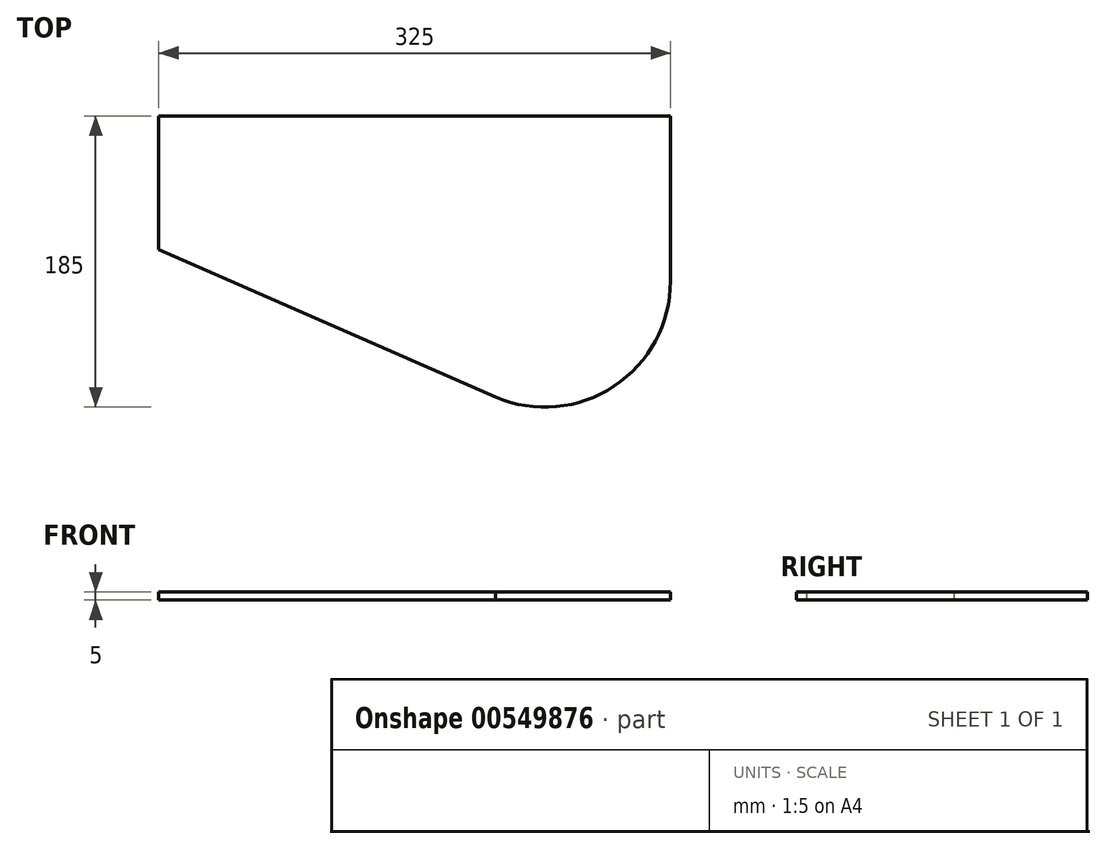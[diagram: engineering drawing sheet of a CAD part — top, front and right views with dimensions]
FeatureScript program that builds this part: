
annotation { "Feature Type Name" : "Feature", "Feature Type Description" : "" }
export const myFeature = defineFeature(function(context is Context, id is Id, definition is map)
    precondition{}
    {
        {
            var Q0;
            Q0=qCreatedBy(makeId("Top.planeOp"),FACE);
            var sketch = newSketch(context, id + "F0", { "sketchPlane" : qUnion([Q0])});
            skLineSegment(sketch, "E0.top", {"start": v(162.5, 92.5) * mm, "end": v(-162.5, 92.5) * mm});
            skPoint(sketch, "E0.middle", {"position": v(0, 0) * mm});
            skArc(sketch, "E1", {"start": v(162.5, -12.5) * mm, "mid": v(126.72, -79.17) * mm, "end": v(51.38, -86.2) * mm});
            skLineSegment(sketch, "E2.left", {"start": v(-162.5, 92.5) * mm, "end": v(-162.5, 7.5) * mm});
            skLineSegment(sketch, "E3", {"start": v(-162.5, 7.5) * mm, "end": v(51.38, -86.2) * mm});
            skLineSegment(sketch, "E4", {"start": v(162.5, 92.5) * mm, "end": v(162.5, -12.5) * mm});
            skSolve(sketch);
        }
        {
            var Q0;
            Q0=makeQuery(id+"F0.imprint","IMPRINT",FACE,{"disambiguationData":[TD([[makeQuery(id+"F0.imprint","IMPRINT",EDGE,{"derivedFrom":sQuery(id+"F0.wireOp",EDGE,"E0.top")}),1.0]])]});
            extrude(context, id + "F1", {"entities" : qUnion([Q0]), "depth" : 5 * mm, "offsetDistance" : 25 * mm});
        }
    });
